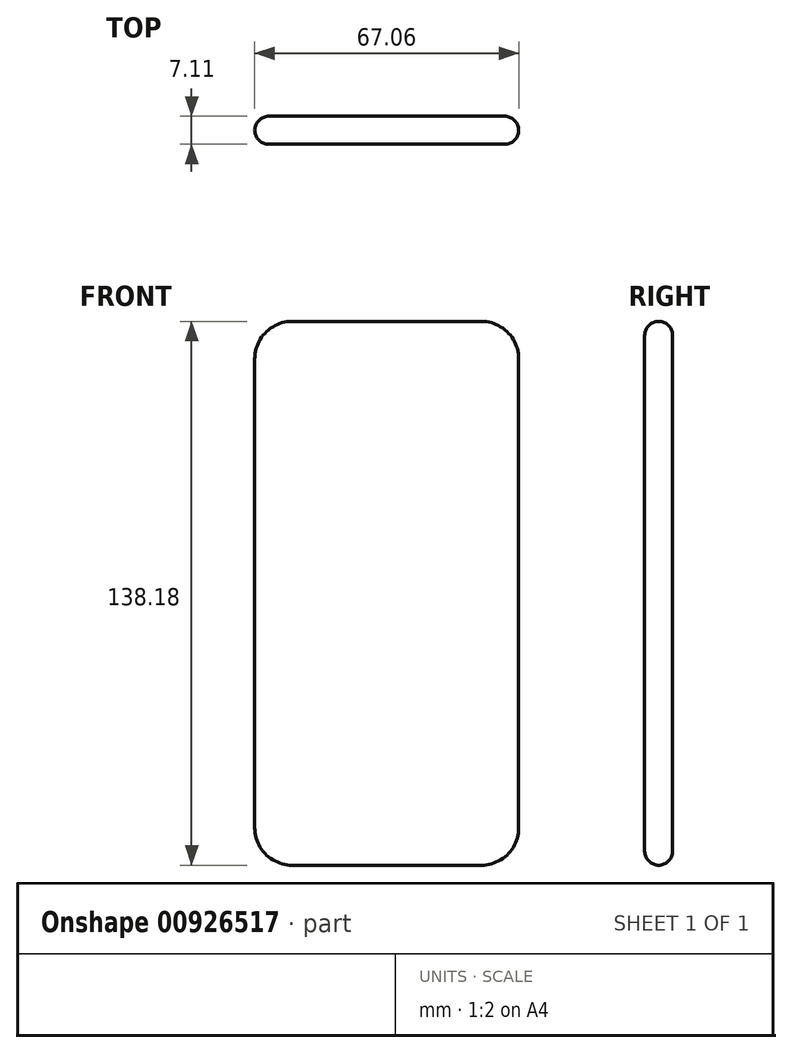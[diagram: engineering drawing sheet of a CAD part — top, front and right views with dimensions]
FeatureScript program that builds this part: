
annotation { "Feature Type Name" : "Feature", "Feature Type Description" : "" }
export const myFeature = defineFeature(function(context is Context, id is Id, definition is map)
    precondition{}
    {
        {
            var Q0;
            Q0=qCreatedBy(makeId("Front.planeOp"),FACE);
            var sketch = newSketch(context, id + "F0", { "sketchPlane" : qUnion([Q0])});
            skLineSegment(sketch, "E0.bottom", {"start": v(33.53, 69.09) * mm, "end": v(-33.53, 69.09) * mm});
            skLineSegment(sketch, "E0.top", {"start": v(33.53, -69.09) * mm, "end": v(-33.53, -69.09) * mm});
            skLineSegment(sketch, "E0.left", {"start": v(33.53, 69.09) * mm, "end": v(33.53, -69.09) * mm});
            skLineSegment(sketch, "E0.right", {"start": v(-33.53, 69.09) * mm, "end": v(-33.53, -69.09) * mm});
            skPoint(sketch, "E0.middle", {"position": v(0, 0) * mm});
            skSolve(sketch);
        }
        {
            var Q0;
            Q0=makeQuery(id+"F0.imprint","IMPRINT",FACE,{"disambiguationData":[TD([[makeQuery(id+"F0.imprint","IMPRINT",EDGE,{"derivedFrom":sQuery(id+"F0.wireOp",EDGE,"E0.bottom")}),1.0]])]});
            extrude(context, id + "F1", {"entities" : qUnion([Q0]), "depth" : 7.11 * mm, "offsetDistance" : 25.4 * mm});
        }
        {
            var Q0;
            Q0=makeQuery(id+"F1.opExtrude","SWEPT_EDGE",EDGE,{"disambiguationData":[OSD([sQuery(id+"F0.wireOp",EDGE,"E0.bottom"),sQuery(id+"F0.wireOp",EDGE,"E0.right")])]});
            var Q1;
            Q1=makeQuery(id+"F1.opExtrude","SWEPT_EDGE",EDGE,{"disambiguationData":[OSD([sQuery(id+"F0.wireOp",EDGE,"E0.bottom"),sQuery(id+"F0.wireOp",EDGE,"E0.left")])]});
            var Q2;
            Q2=makeQuery(id+"F1.opExtrude","SWEPT_EDGE",EDGE,{"disambiguationData":[OSD([sQuery(id+"F0.wireOp",EDGE,"E0.top"),sQuery(id+"F0.wireOp",EDGE,"E0.left")])]});
            var Q3;
            Q3=makeQuery(id+"F1.opExtrude","SWEPT_EDGE",EDGE,{"disambiguationData":[OSD([sQuery(id+"F0.wireOp",EDGE,"E0.top"),sQuery(id+"F0.wireOp",EDGE,"E0.right")])]});
            fillet(context, id + "F2", {"entities" : qUnion([Q0, Q1, Q2, Q3]), "radius" : 9.52 * mm, "tangentPropagation" : true, "allowEdgeOverflow" : false});
        }
        {
            var Q0;
            Q0=makeQuery(id+"F1.opExtrude","CAP_FACE",FACE,{"disambiguationData":[OSD([sQuery(id+"F0.wireOp",EDGE,"E0.bottom"),sQuery(id+"F0.wireOp",EDGE,"E0.top"),sQuery(id+"F0.wireOp",EDGE,"E0.left"),sQuery(id+"F0.wireOp",EDGE,"E0.right")])],"isStart":false});
            var Q1;
            Q1=makeQuery(id+"F1.opExtrude","CAP_FACE",FACE,{"disambiguationData":[OSD([sQuery(id+"F0.wireOp",EDGE,"E0.bottom"),sQuery(id+"F0.wireOp",EDGE,"E0.top"),sQuery(id+"F0.wireOp",EDGE,"E0.left"),sQuery(id+"F0.wireOp",EDGE,"E0.right")])],"isStart":true});
            fillet(context, id + "F3", {"entities" : qUnion([Q0, Q1]), "radius" : 3.56 * mm, "tangentPropagation" : true, "allowEdgeOverflow" : false});
        }
    });
